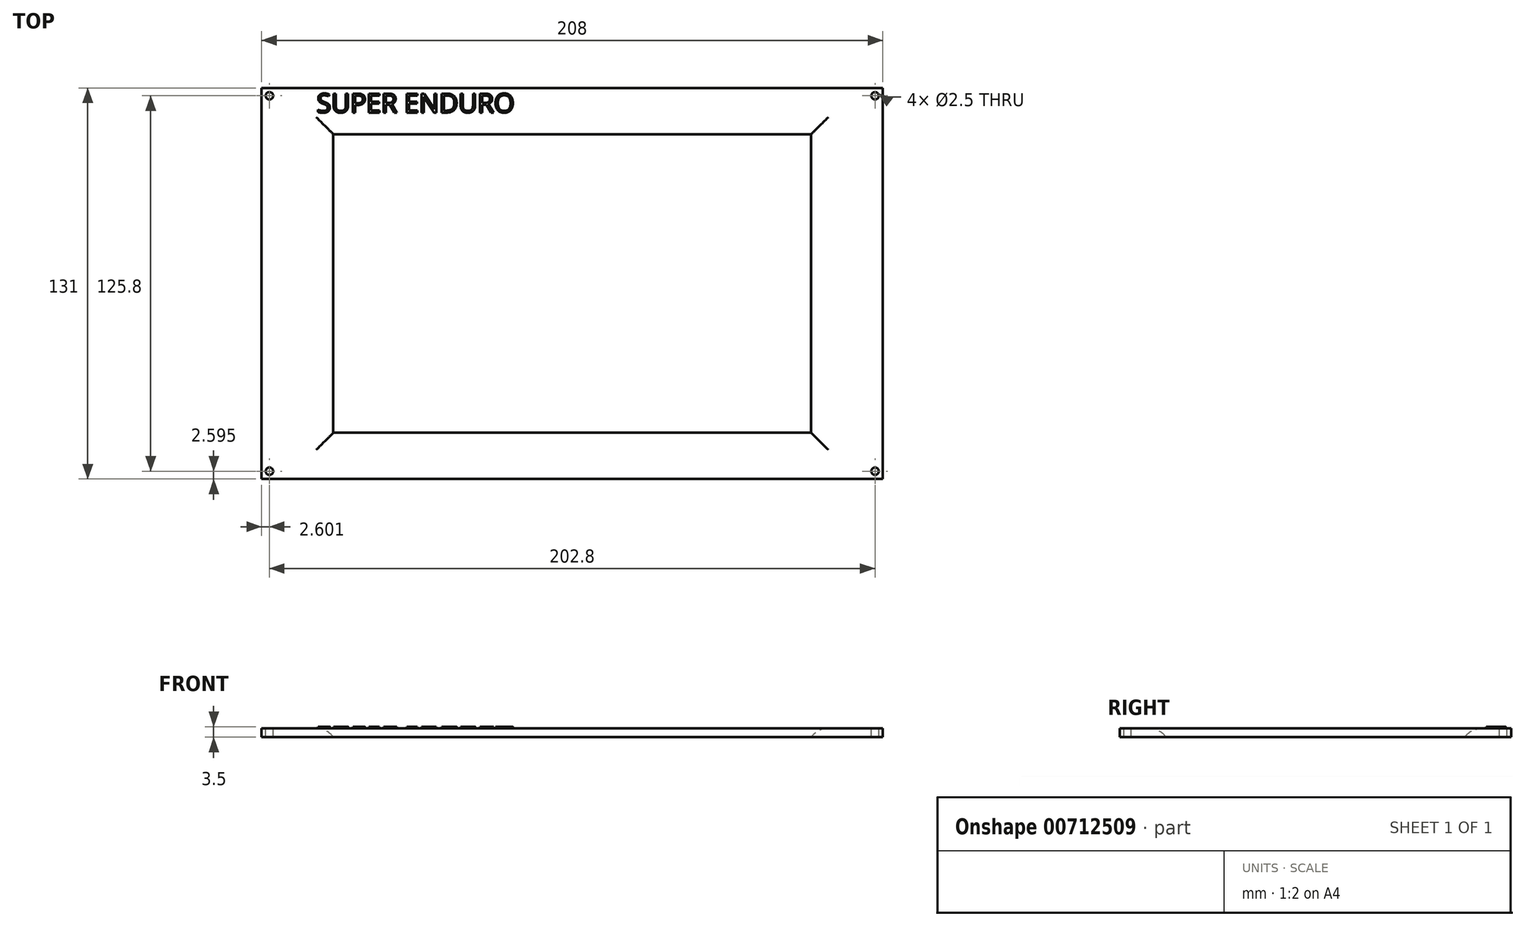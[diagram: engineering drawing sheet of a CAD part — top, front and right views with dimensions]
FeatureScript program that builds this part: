
annotation { "Feature Type Name" : "Feature", "Feature Type Description" : "" }
export const myFeature = defineFeature(function(context is Context, id is Id, definition is map)
    precondition{}
    {
        {
            var Q0;
            Q0=qCreatedBy(makeId("Top.planeOp"),FACE);
            var sketch = newSketch(context, id + "F0", { "sketchPlane" : qUnion([Q0])});
            skLineSegment(sketch, "E0.bottom", {"start": v(-83.47, 57.26) * mm, "end": v(124.53, 57.26) * mm});
            skLineSegment(sketch, "E0.top", {"start": v(-83.47, -73.74) * mm, "end": v(124.53, -73.74) * mm});
            skLineSegment(sketch, "E0.left", {"start": v(-83.47, 57.26) * mm, "end": v(-83.47, -73.74) * mm});
            skLineSegment(sketch, "E0.right", {"start": v(124.53, 57.26) * mm, "end": v(124.53, -73.74) * mm});
            skLineSegment(sketch, "E1.bottom", {"start": v(-59.47, 41.76) * mm, "end": v(100.53, 41.76) * mm});
            skLineSegment(sketch, "E1.top", {"start": v(-59.47, -58.24) * mm, "end": v(100.53, -58.24) * mm});
            skLineSegment(sketch, "E1.left", {"start": v(-59.47, 41.76) * mm, "end": v(-59.47, -58.24) * mm});
            skLineSegment(sketch, "E1.right", {"start": v(100.53, 41.76) * mm, "end": v(100.53, -58.24) * mm});
            skSolve(sketch);
        }
        {
            var Q0;
            Q0 = qSketchRegion(id + "F0", true);
            extrude(context, id + "F1", {"entities" : qUnion([Q0]), "depth" : 3 * mm, "offsetDistance" : 25 * mm});
        }
        {
            var Q0;
            Q0=makeQuery(id+"F1.opExtrude","CAP_EDGE",EDGE,{"disambiguationData":[OSD([sQuery(id+"F0.wireOp",EDGE,"E1.bottom")])],"isStart":false});
            var Q1;
            Q1=makeQuery(id+"F1.opExtrude","CAP_EDGE",EDGE,{"disambiguationData":[OSD([sQuery(id+"F0.wireOp",EDGE,"E1.left")])],"isStart":false});
            var Q2;
            Q2=makeQuery(id+"F1.opExtrude","CAP_EDGE",EDGE,{"disambiguationData":[OSD([sQuery(id+"F0.wireOp",EDGE,"E1.top")])],"isStart":false});
            var Q3;
            Q3=makeQuery(id+"F1.opExtrude","CAP_EDGE",EDGE,{"disambiguationData":[OSD([sQuery(id+"F0.wireOp",EDGE,"E1.right")])],"isStart":false});
            fillet(context, id + "F2", {"entities" : qUnion([Q0, Q1, Q2, Q3]), "radius" : 7 * mm, "tangentPropagation" : true, "allowEdgeOverflow" : false});
        }
        {
            var Q0;
            Q0=makeQuery(id+"F1.opExtrude","CAP_FACE",FACE,{"disambiguationData":[OSD([sQuery(id+"F0.wireOp",EDGE,"E0.bottom"),sQuery(id+"F0.wireOp",EDGE,"E0.top"),sQuery(id+"F0.wireOp",EDGE,"E0.left"),sQuery(id+"F0.wireOp",EDGE,"E0.right"),sQuery(id+"F0.wireOp",EDGE,"E1.bottom"),sQuery(id+"F0.wireOp",EDGE,"E1.top"),sQuery(id+"F0.wireOp",EDGE,"E1.left"),sQuery(id+"F0.wireOp",EDGE,"E1.right")])],"isStart":false});
            var sketch = newSketch(context, id + "F3", { "sketchPlane" : qUnion([Q0])});
            skPoint(sketch, "E2", {"position": v(-80.87, 54.66) * mm});
            skPoint(sketch, "E3", {"position": v(121.93, 54.66) * mm});
            skPoint(sketch, "E4", {"position": v(121.93, -71.14) * mm});
            skPoint(sketch, "E5", {"position": v(-80.87, -71.14) * mm});
            skSolve(sketch);
        }
        {
            var Q0;
            Q0=sQuery(id+"F3.wireOp",VERTEX,"E2");
            var Q1;
            Q1=sQuery(id+"F3.wireOp",VERTEX,"E3");
            var Q2;
            Q2=sQuery(id+"F3.wireOp",VERTEX,"E4");
            var Q3;
            Q3=sQuery(id+"F3.wireOp",VERTEX,"E5");
            var Q4;
            Q4=makeQuery(id+"F1.opExtrude","SWEPT_BODY",BODY,{"disambiguationData":[OSD([sQuery(id+"F0.wireOp",EDGE,"E0.bottom"),sQuery(id+"F0.wireOp",EDGE,"E0.top"),sQuery(id+"F0.wireOp",EDGE,"E0.left"),sQuery(id+"F0.wireOp",EDGE,"E0.right"),sQuery(id+"F0.wireOp",EDGE,"E1.bottom"),sQuery(id+"F0.wireOp",EDGE,"E1.top"),sQuery(id+"F0.wireOp",EDGE,"E1.left"),sQuery(id+"F0.wireOp",EDGE,"E1.right")])]});
            hole(context, id + "F4", {"style" : HoleStyle.SIMPLE, "endStyle" : HoleEndStyle.BLIND, "holeDiameter" : 2.5 * mm, "majorDiameter" : 5 * mm, "holeDepth" : 12 * mm, "isTappedThrough" : true, "tappedDepth" : 12 * mm, "tapClearance" : 3, "locations" : qUnion([Q0, Q1, Q2, Q3]), "scope" : qUnion([Q4])});
        }
        {
            var Q0;
            Q0=makeQuery(id+"F1.opExtrude","CAP_FACE",FACE,{"disambiguationData":[OSD([sQuery(id+"F0.wireOp",EDGE,"E0.bottom"),sQuery(id+"F0.wireOp",EDGE,"E0.top"),sQuery(id+"F0.wireOp",EDGE,"E0.left"),sQuery(id+"F0.wireOp",EDGE,"E0.right"),sQuery(id+"F0.wireOp",EDGE,"E1.bottom"),sQuery(id+"F0.wireOp",EDGE,"E1.top"),sQuery(id+"F0.wireOp",EDGE,"E1.left"),sQuery(id+"F0.wireOp",EDGE,"E1.right")])],"isStart":false});
            var sketch = newSketch(context, id + "F5", { "sketchPlane" : qUnion([Q0])});
            skText(sketch, "E6", { "text": "SUPER ENDURO", "fontName": "OpenSans-Regular.ttf"});
            const initialGuessF5  = {"E6": [-0.06506, 0.04903, 1, 0, 0.00638]};
            skSetInitialGuess(sketch, initialGuessF5);
            skSolve(sketch);
        }
        {
            var Q0;
            Q0 = qSketchRegion(id + "F5", true);
            extrude(context, id + "F6", {"entities" : qUnion([Q0]), "operationType" : NewBodyOperationType.ADD, "depth" : 0.5 * mm, "offsetDistance" : 25 * mm});
        }
    });
